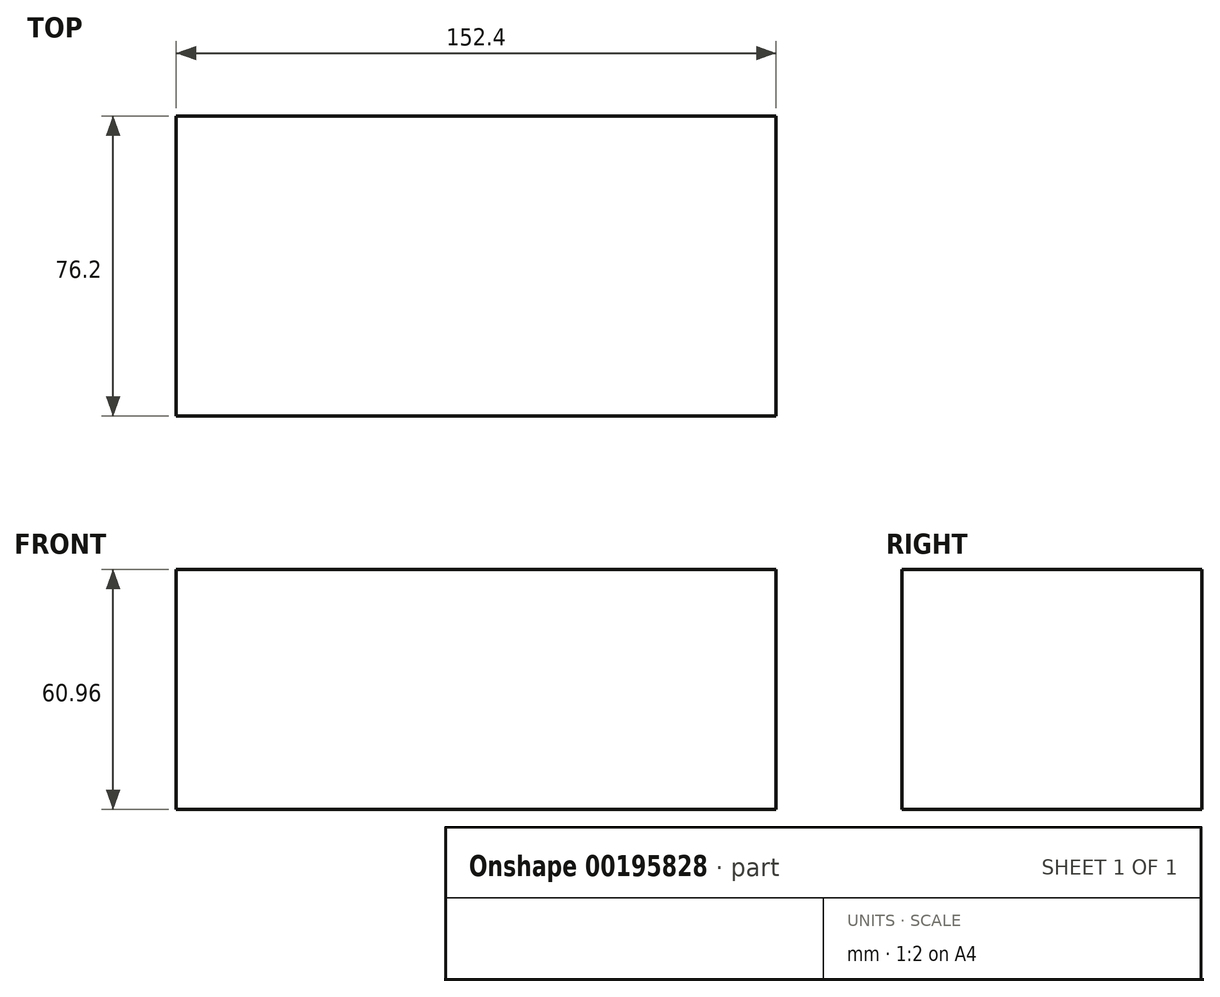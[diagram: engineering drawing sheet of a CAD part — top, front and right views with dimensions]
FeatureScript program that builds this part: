
annotation { "Feature Type Name" : "Feature", "Feature Type Description" : "" }
export const myFeature = defineFeature(function(context is Context, id is Id, definition is map)
    precondition{}
    {
        {
            var Q0;
            Q0=qCreatedBy(makeId("Top.planeOp"),FACE);
            var sketch = newSketch(context, id + "F0", { "sketchPlane" : qUnion([Q0])});
            skLineSegment(sketch, "E0.bottom", {"start": v(-74.27, 38.1) * mm, "end": v(78.13, 38.1) * mm});
            skLineSegment(sketch, "E0.top", {"start": v(-74.27, -38.1) * mm, "end": v(78.13, -38.1) * mm});
            skLineSegment(sketch, "E0.left", {"start": v(-74.27, 38.1) * mm, "end": v(-74.27, -38.1) * mm});
            skLineSegment(sketch, "E0.right", {"start": v(78.13, 38.1) * mm, "end": v(78.13, -38.1) * mm});
            skPoint(sketch, "E0.middle", {"position": v(1.93, 0) * mm});
            skSolve(sketch);
        }
        {
            var Q0;
            Q0=makeQuery(id+"F0.imprint","IMPRINT",FACE,{"disambiguationData":[TD([[makeQuery(id+"F0.imprint","IMPRINT",EDGE,{"derivedFrom":sQuery(id+"F0.wireOp",EDGE,"E0.bottom")}),-1.0]])]});
            extrude(context, id + "F1", {"entities" : qUnion([Q0]), "depth" : 60.96 * mm});
        }
    });
